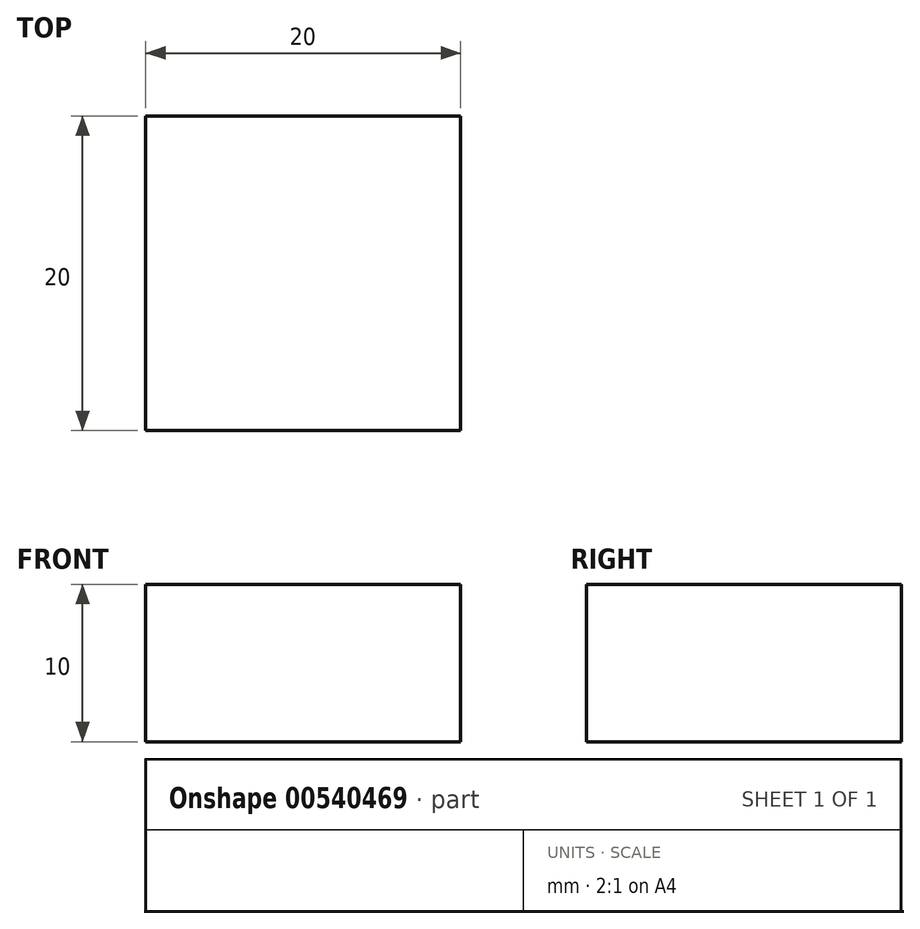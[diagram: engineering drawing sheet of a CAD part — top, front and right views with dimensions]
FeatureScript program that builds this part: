
annotation { "Feature Type Name" : "Feature", "Feature Type Description" : "" }
export const myFeature = defineFeature(function(context is Context, id is Id, definition is map)
    precondition{}
    {
        {
            var Q0;
            Q0=qCreatedBy(makeId("Top.planeOp"),FACE);
            var sketch = newSketch(context, id + "F0", { "sketchPlane" : qUnion([Q0])});
            skLineSegment(sketch, "E0.bottom", {"start": v(10, 10) * mm, "end": v(-10, 10) * mm});
            skLineSegment(sketch, "E0.top", {"start": v(10, -10) * mm, "end": v(-10, -10) * mm});
            skLineSegment(sketch, "E0.left", {"start": v(10, 10) * mm, "end": v(10, -10) * mm});
            skLineSegment(sketch, "E0.right", {"start": v(-10, 10) * mm, "end": v(-10, -10) * mm});
            skPoint(sketch, "E0.middle", {"position": v(0, 0) * mm});
            skSolve(sketch);
        }
        {
            var Q0;
            Q0=makeQuery(id+"F0.imprint","IMPRINT",FACE,{"disambiguationData":[TD([[makeQuery(id+"F0.imprint","IMPRINT",EDGE,{"derivedFrom":sQuery(id+"F0.wireOp",EDGE,"E0.bottom")}),1.0]])]});
            extrude(context, id + "F1", {"entities" : qUnion([Q0]), "depth" : 10 * mm, "offsetDistance" : 25 * mm});
        }
    });
